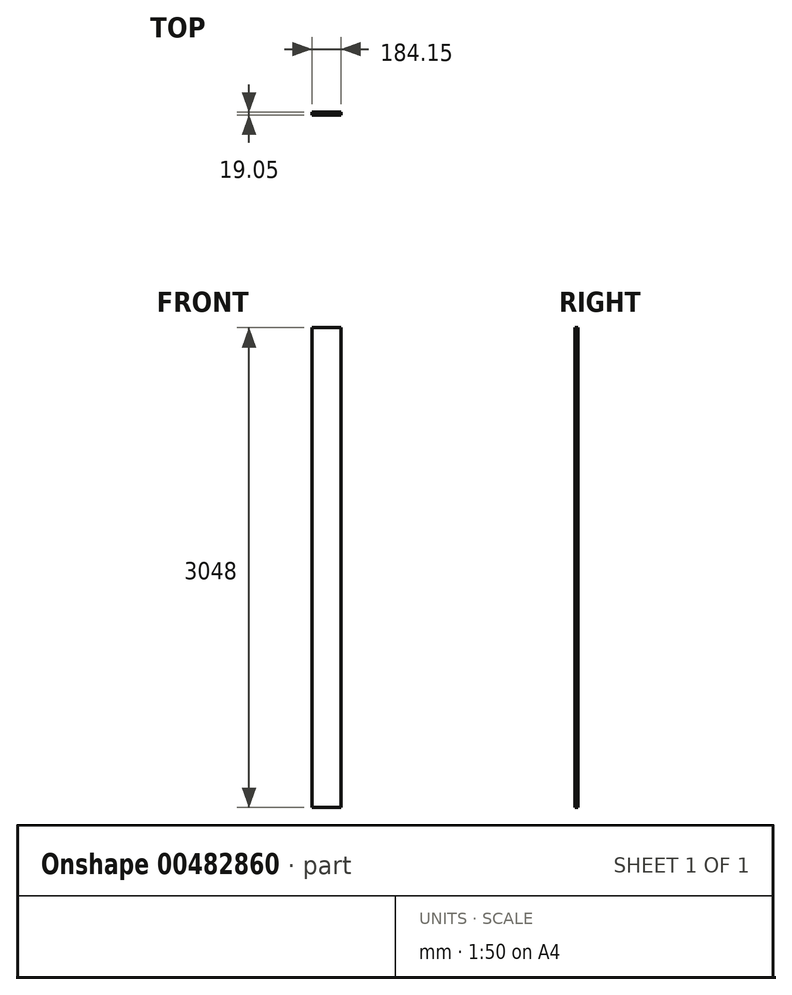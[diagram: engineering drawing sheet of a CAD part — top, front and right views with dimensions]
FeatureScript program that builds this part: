
annotation { "Feature Type Name" : "Feature", "Feature Type Description" : "" }
export const myFeature = defineFeature(function(context is Context, id is Id, definition is map)
    precondition{}
    {
        {
            var Q0;
            Q0=qCreatedBy(makeId("Front.planeOp"),FACE);
            var sketch = newSketch(context, id + "F0", { "sketchPlane" : qUnion([Q0])});
            skLineSegment(sketch, "E0.bottom", {"start": v(0, 3048) * mm, "end": v(184.15, 3048) * mm});
            skLineSegment(sketch, "E0.top", {"start": v(0, 0) * mm, "end": v(184.15, 0) * mm});
            skLineSegment(sketch, "E0.left", {"start": v(0, 3048) * mm, "end": v(0, 0) * mm});
            skLineSegment(sketch, "E0.right", {"start": v(184.15, 3048) * mm, "end": v(184.15, 0) * mm});
            skSolve(sketch);
        }
        {
            var Q0;
            Q0 = qSketchRegion(id + "F0", true);
            extrude(context, id + "F1", {"entities" : qUnion([Q0]), "depth" : 19.05 * mm});
        }
    });
